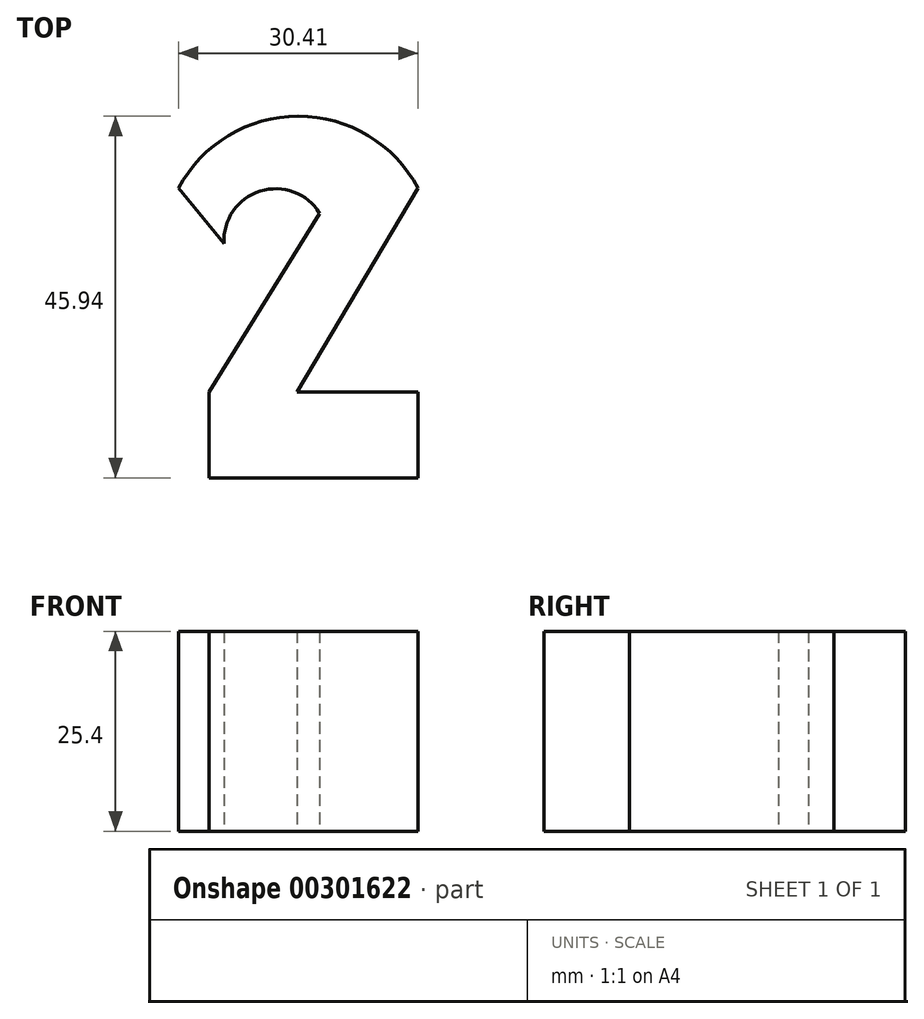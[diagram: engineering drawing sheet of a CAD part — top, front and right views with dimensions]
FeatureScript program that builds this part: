
annotation { "Feature Type Name" : "Feature", "Feature Type Description" : "" }
export const myFeature = defineFeature(function(context is Context, id is Id, definition is map)
    precondition{}
    {
        {
            var Q0;
            Q0=qCreatedBy(makeId("Top.planeOp"),FACE);
            var sketch = newSketch(context, id + "F0", { "sketchPlane" : qUnion([Q0])});
            skArc(sketch, "E0", {"start": v(44.17, 25.92) * mm, "mid": v(28.96, 35.06) * mm, "end": v(13.76, 25.92) * mm});
            skLineSegment(sketch, "E1", {"start": v(44.17, 25.92) * mm, "end": v(28.8, 0) * mm});
            skLineSegment(sketch, "E2", {"start": v(28.8, 0) * mm, "end": v(44.17, 0) * mm});
            skLineSegment(sketch, "E3", {"start": v(44.17, 0) * mm, "end": v(44.17, -10.88) * mm});
            skLineSegment(sketch, "E4", {"start": v(44.17, -10.88) * mm, "end": v(17.6, -10.88) * mm});
            skLineSegment(sketch, "E5", {"start": v(17.6, -10.88) * mm, "end": v(17.6, 0) * mm});
            skLineSegment(sketch, "E6", {"start": v(17.6, 0) * mm, "end": v(31.68, 22.72) * mm});
            skLineSegment(sketch, "E7", {"start": v(13.76, 25.92) * mm, "end": v(19.52, 18.88) * mm});
            skArc(sketch, "E8", {"start": v(31.68, 22.72) * mm, "mid": v(24.1, 25.54) * mm, "end": v(19.52, 18.88) * mm});
            skSolve(sketch);
        }
        {
            var Q0;
            Q0=makeQuery(id+"F0.imprint","IMPRINT",FACE,{"disambiguationData":[TD([[makeQuery(id+"F0.imprint","IMPRINT",EDGE,{"derivedFrom":sQuery(id+"F0.wireOp",EDGE,"E0")}),1.0]])]});
            extrude(context, id + "F1", {"entities" : qUnion([Q0]), "depth" : 25.4 * mm});
        }
    });
